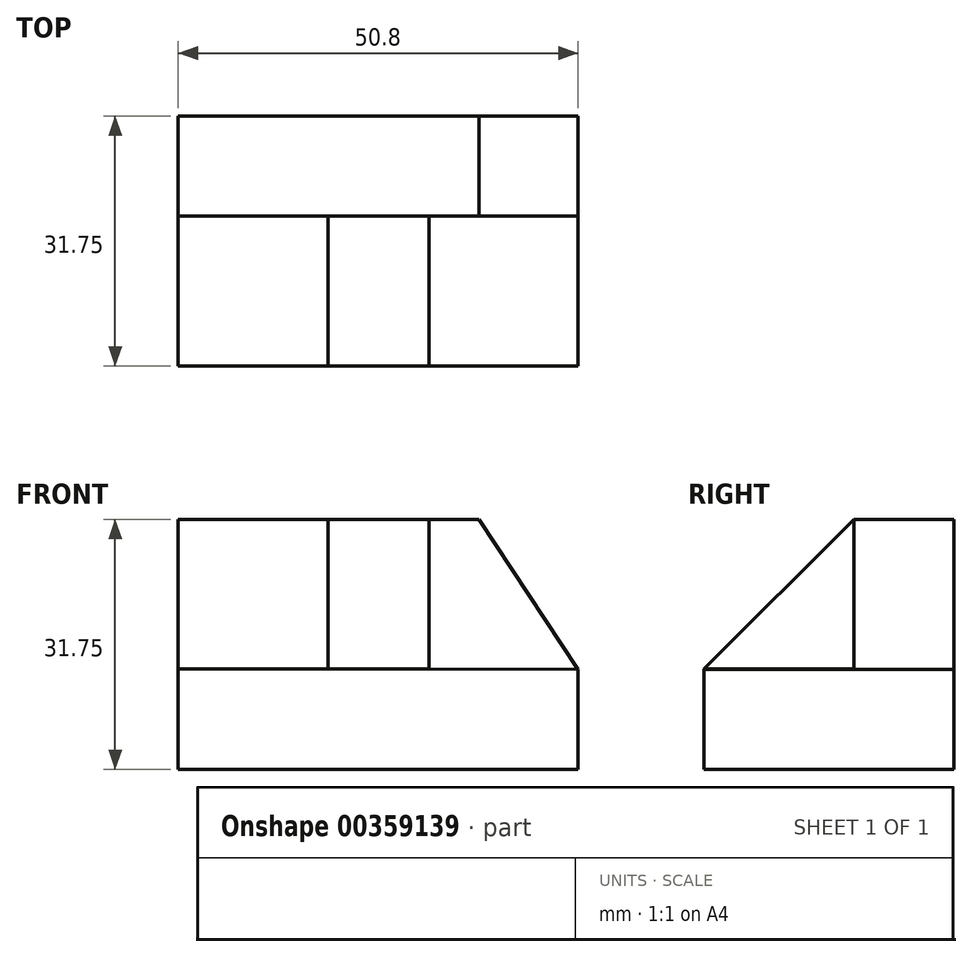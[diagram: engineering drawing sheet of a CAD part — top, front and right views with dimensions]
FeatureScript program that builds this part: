
annotation { "Feature Type Name" : "Feature", "Feature Type Description" : "" }
export const myFeature = defineFeature(function(context is Context, id is Id, definition is map)
    precondition{}
    {
        {
            var Q0;
            Q0=qCreatedBy(makeId("Front.planeOp"),FACE);
            var sketch = newSketch(context, id + "F0", { "sketchPlane" : qUnion([Q0])});
            skLineSegment(sketch, "E0", {"start": v(-38.21, 18.95) * mm, "end": v(-38.21, -12.8) * mm});
            skLineSegment(sketch, "E1", {"start": v(-38.21, -12.8) * mm, "end": v(12.59, -12.8) * mm});
            skLineSegment(sketch, "E2", {"start": v(12.59, -12.8) * mm, "end": v(12.59, 18.95) * mm});
            skLineSegment(sketch, "E3", {"start": v(12.59, 18.95) * mm, "end": v(-38.21, 18.95) * mm});
            skSolve(sketch);
        }
        {
            var Q0;
            Q0 = qSketchRegion(id + "F0", true);
            extrude(context, id + "F1", {"entities" : qUnion([Q0]), "depth" : 31.75 * mm});
        }
        {
            var Q0;
            Q0=makeQuery(id+"F1.opExtrude","CAP_FACE",FACE,{"disambiguationData":[OSD([sQuery(id+"F0.wireOp",EDGE,"E0"),sQuery(id+"F0.wireOp",EDGE,"E1"),sQuery(id+"F0.wireOp",EDGE,"E2"),sQuery(id+"F0.wireOp",EDGE,"E3")])],"isStart":false});
            var sketch = newSketch(context, id + "F2", { "sketchPlane" : qUnion([Q0])});
            skLineSegment(sketch, "E4", {"start": v(12.59, 18.95) * mm, "end": v(0, 18.95) * mm});
            skLineSegment(sketch, "E5", {"start": v(0, 18.95) * mm, "end": v(12.59, -0.1) * mm});
            skLineSegment(sketch, "E6", {"start": v(12.59, -0.1) * mm, "end": v(12.59, 18.95) * mm});
            skSolve(sketch);
        }
        {
            var Q0;
            Q0 = qSketchRegion(id + "F2", true);
            extrude(context, id + "F3", {"entities" : qUnion([Q0]), "operationType" : NewBodyOperationType.REMOVE, "oppositeDirection" : true, "depth" : 31.75 * mm});
        }
        {
            var Q0;
            Q0=makeQuery(id+"F1.opExtrude","CAP_FACE",FACE,{"disambiguationData":[OSD([sQuery(id+"F0.wireOp",EDGE,"E0"),sQuery(id+"F0.wireOp",EDGE,"E1"),sQuery(id+"F0.wireOp",EDGE,"E2"),sQuery(id+"F0.wireOp",EDGE,"E3")])],"isStart":false});
            var sketch = newSketch(context, id + "F4", { "sketchPlane" : qUnion([Q0])});
            skLineSegment(sketch, "E7", {"start": v(12.59, -0.1) * mm, "end": v(-6.35, 0) * mm});
            skLineSegment(sketch, "E8", {"start": v(-6.35, 0) * mm, "end": v(-6.35, 18.95) * mm});
            skLineSegment(sketch, "E9", {"start": v(-6.35, 18.95) * mm, "end": v(0, 18.95) * mm});
            skLineSegment(sketch, "E10", {"start": v(0, 18.95) * mm, "end": v(12.59, -0.1) * mm});
            skSolve(sketch);
        }
        {
            var Q0;
            Q0 = qSketchRegion(id + "F4", true);
            extrude(context, id + "F5", {"entities" : qUnion([Q0]), "operationType" : NewBodyOperationType.REMOVE, "oppositeDirection" : true, "depth" : 19.05 * mm});
        }
        {
            var Q0;
            Q0=makeQuery(id+"F1.opExtrude","CAP_FACE",FACE,{"disambiguationData":[OSD([sQuery(id+"F0.wireOp",EDGE,"E0"),sQuery(id+"F0.wireOp",EDGE,"E1"),sQuery(id+"F0.wireOp",EDGE,"E2"),sQuery(id+"F0.wireOp",EDGE,"E3")])],"isStart":false});
            var sketch = newSketch(context, id + "F6", { "sketchPlane" : qUnion([Q0])});
            skLineSegment(sketch, "E11", {"start": v(-38.21, 18.95) * mm, "end": v(-38.21, 0) * mm});
            skLineSegment(sketch, "E12", {"start": v(-38.21, 0) * mm, "end": v(-19.16, 0) * mm});
            skLineSegment(sketch, "E13", {"start": v(-19.16, 0) * mm, "end": v(-19.16, 18.95) * mm});
            skLineSegment(sketch, "E14", {"start": v(-19.16, 18.95) * mm, "end": v(-38.21, 18.95) * mm});
            skSolve(sketch);
        }
        {
            var Q0;
            Q0 = qSketchRegion(id + "F6", true);
            extrude(context, id + "F7", {"entities" : qUnion([Q0]), "operationType" : NewBodyOperationType.REMOVE, "oppositeDirection" : true, "depth" : 19.05 * mm});
        }
        {
            var Q0;
            Q0=makeQuery(id+"F5.boolean.opBoolean","COPY",FACE,{"derivedFrom":makeQuery(id+"F5.opExtrude","SWEPT_FACE",FACE,{"disambiguationData":[OSD([sQuery(id+"F4.wireOp",EDGE,"E8")])]})});
            var sketch = newSketch(context, id + "F8", { "sketchPlane" : qUnion([Q0])});
            skLineSegment(sketch, "E15", {"start": v(-12.7, 18.95) * mm, "end": v(-31.75, 0) * mm});
            skLineSegment(sketch, "E16", {"start": v(-31.75, 0) * mm, "end": v(-31.75, 18.95) * mm});
            skLineSegment(sketch, "E17", {"start": v(-31.75, 18.95) * mm, "end": v(-12.7, 18.95) * mm});
            skSolve(sketch);
        }
        {
            var Q0;
            Q0 = qSketchRegion(id + "F8", true);
            extrude(context, id + "F9", {"entities" : qUnion([Q0]), "operationType" : NewBodyOperationType.REMOVE, "oppositeDirection" : true, "depth" : 12.7 * mm});
        }
        {
            var Q0;
            Q0=makeQuery(id+"F7.boolean.opBoolean","COPY",FACE,{"derivedFrom":makeQuery(id+"F7.opExtrude","SWEPT_FACE",FACE,{"disambiguationData":[OSD([sQuery(id+"F6.wireOp",EDGE,"E13")])]})});
            var sketch = newSketch(context, id + "F10", { "sketchPlane" : qUnion([Q0])});
            skLineSegment(sketch, "E18", {"start": v(12.7, 18.95) * mm, "end": v(31.75, 0) * mm});
            skLineSegment(sketch, "E19", {"start": v(31.75, 0) * mm, "end": v(31.75, 18.95) * mm});
            skLineSegment(sketch, "E20", {"start": v(31.75, 18.95) * mm, "end": v(12.7, 18.95) * mm});
            skSolve(sketch);
        }
        {
            var Q0;
            Q0=makeQuery(id+"F10.imprint","IMPRINT",FACE,{"disambiguationData":[TD([[makeQuery(id+"F10.imprint","IMPRINT",EDGE,{"derivedFrom":sQuery(id+"F10.wireOp",EDGE,"E18")}),1.0]])]});
            extrude(context, id + "F11", {"entities" : qUnion([Q0]), "operationType" : NewBodyOperationType.REMOVE, "oppositeDirection" : true, "depth" : 25.4 * mm});
        }
    });
